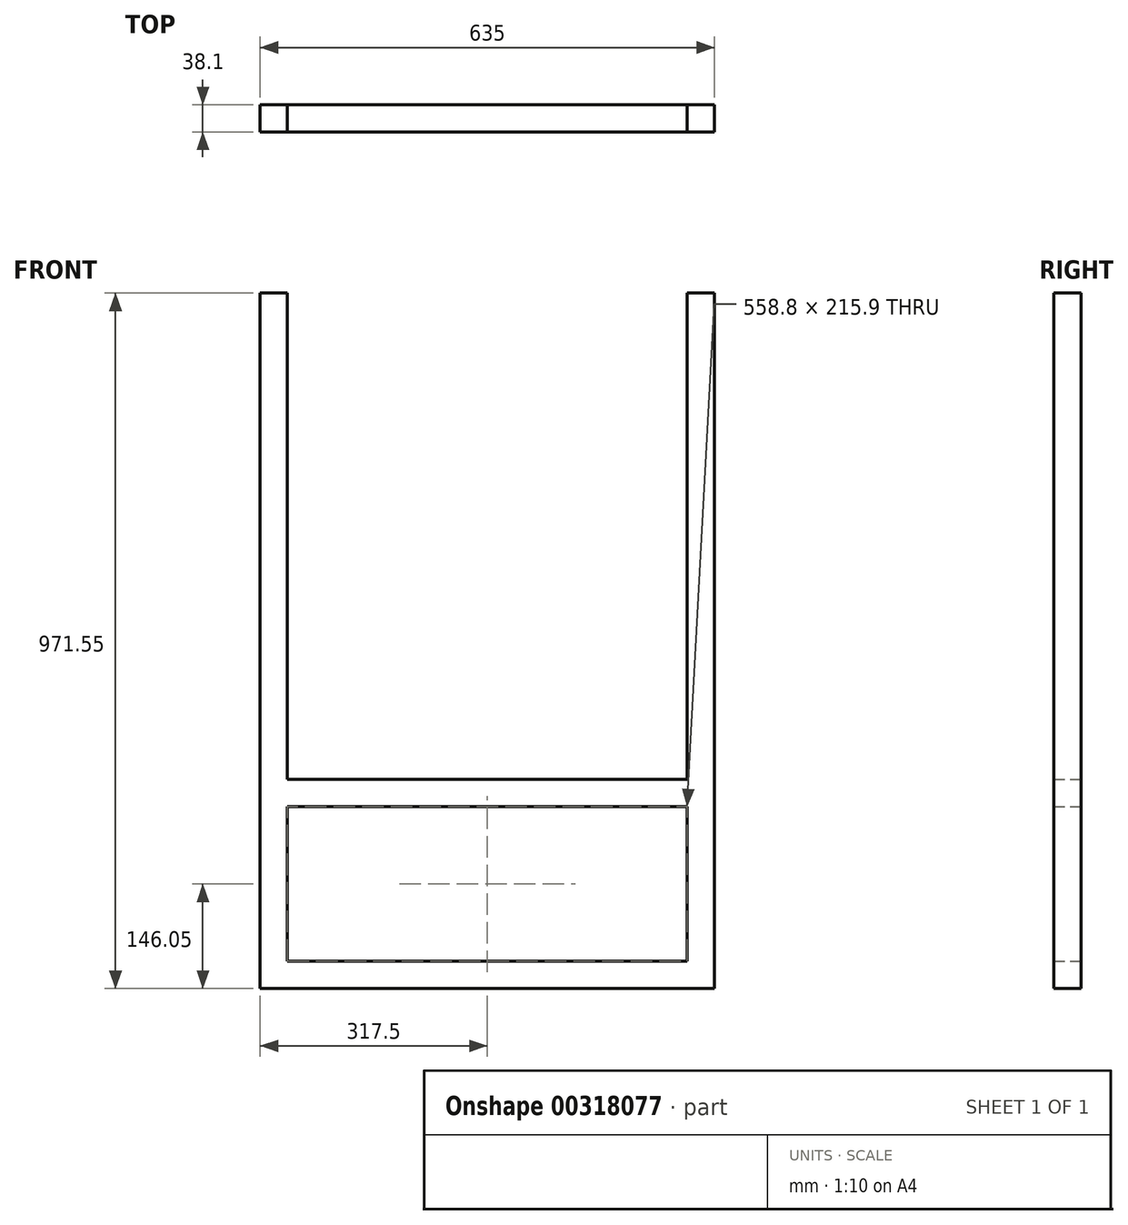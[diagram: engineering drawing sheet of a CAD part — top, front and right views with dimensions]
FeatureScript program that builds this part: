
annotation { "Feature Type Name" : "Feature", "Feature Type Description" : "" }
export const myFeature = defineFeature(function(context is Context, id is Id, definition is map)
    precondition{}
    {
        {
            var Q0;
            Q0=qCreatedBy(makeId("Front.planeOp"),FACE);
            var sketch = newSketch(context, id + "F0", { "sketchPlane" : qUnion([Q0])});
            skLineSegment(sketch, "E0.0", {"start": v(38.1, 38.1) * mm, "end": v(596.9, 38.1) * mm});
            skLineSegment(sketch, "E0.1", {"start": v(38.1, 38.1) * mm, "end": v(38.1, 254) * mm});
            skLineSegment(sketch, "E0.2", {"start": v(38.1, 254) * mm, "end": v(596.9, 254) * mm});
            skLineSegment(sketch, "E0.3", {"start": v(596.9, 38.1) * mm, "end": v(596.9, 254) * mm});
            skLineSegment(sketch, "E1.0.1.4", {"start": v(38.1, 292.1) * mm, "end": v(596.9, 292.1) * mm});
            skLineSegment(sketch, "E1.0.1.5", {"start": v(38.1, 292.1) * mm, "end": v(38.1, 971.55) * mm});
            skLineSegment(sketch, "E1.0.1.7", {"start": v(596.9, 292.1) * mm, "end": v(596.9, 971.55) * mm});
            skLineSegment(sketch, "E2.top", {"start": v(0, 0) * mm, "end": v(635, 0) * mm});
            skLineSegment(sketch, "E2.left", {"start": v(0, 971.55) * mm, "end": v(0, 0) * mm});
            skLineSegment(sketch, "E2.right", {"start": v(635, 971.55) * mm, "end": v(635, 0) * mm});
            skLineSegment(sketch, "E3", {"start": v(0, 971.55) * mm, "end": v(38.1, 971.55) * mm});
            skLineSegment(sketch, "E4", {"start": v(596.9, 971.55) * mm, "end": v(635, 971.55) * mm});
            skSolve(sketch);
        }
        {
            var Q0;
            Q0=makeQuery(id+"F0.imprint","IMPRINT",FACE,{"disambiguationData":[TD([[makeQuery(id+"F0.imprint","IMPRINT",EDGE,{"derivedFrom":sQuery(id+"F0.wireOp",EDGE,"E0.0")}),-1.0]])]});
            extrude(context, id + "F1", {"entities" : qUnion([Q0]), "depth" : 38.1 * mm, "offsetDistance" : 25.4 * mm});
        }
    });
